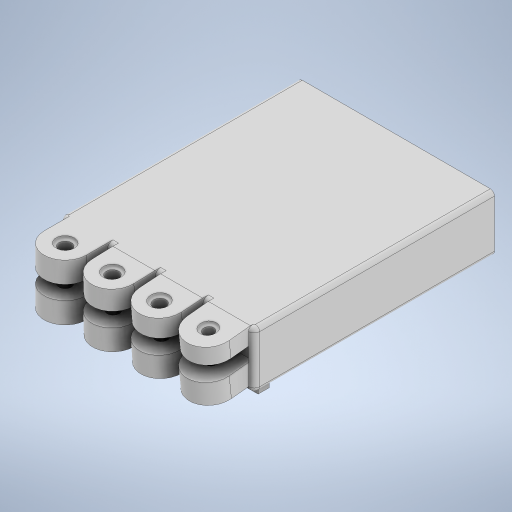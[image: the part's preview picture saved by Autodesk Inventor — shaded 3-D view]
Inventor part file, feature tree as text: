
AUTODESK INVENTOR PART (.ipt)
format: ipt  version: 2024 (Build 280153000, 153)  size: 733,184 bytes
history: native  units: mm
features: sketch x18, extrude x17, fillet x9, other x1
ambient origin geometry x8: Origin, YZ Plane, XZ Plane, XY Plane, X Axis, Y Axis, Z Axis, Center Point
bodies: Body1 (feature_tree)
feature tree (45):
  other  "Твердое тело1"
  extrude  "Выдавливание1"  Depth=20.0mm
  extrude  "Выдавливание2"  Depth=100.0mm
  extrude  "Выдавливание3"  Depth=15.0mm
  extrude  "Выдавливание4"  Depth=5.0mm
  extrude  "Выдавливание5"  Depth=7.5mm
  extrude  "Выдавливание6"  Depth=7.5mm
  extrude  "Выдавливание7"  Depth=15.0mm TaperAngle=0.0deg
  extrude  "Выдавливание8"  Depth=85.0mm
  extrude  "Выдавливание9"  Depth=2.0mm TaperAngle=0.0deg
  extrude  "Выдавливание10"  Depth=15.358897mm
  extrude  "Выдавливание11"  TaperAngle=90.0deg  [1 undecoded]
  sketch  "Эскиз12"
  extrude  "Выдавливание12"  Depth=15.358897mm
  extrude  "Выдавливание13"  Depth=15.0mm
  extrude  "Выдавливание14"  Depth=5.0mm
  extrude  "Выдавливание15"  Depth=7.496951mm
  extrude  "Выдавливание16"  Depth=7.496951mm
  fillet  "Сопряжение1"  Radius=0.349066mm
  fillet  "Сопряжение2"  Radius=15.0mm
  fillet  "Сопряжение3"  Radius=2.0mm
  fillet  "Сопряжение4"  [1 undecoded]
  fillet  "Сопряжение5"  [1 undecoded]
  fillet  "Сопряжение6"  Radius=15.009832mm
  fillet  "Сопряжение7"  Radius=15.009832mm
  fillet  "Сопряжение8"  Radius=5.0mm
  extrude  "Выдавливание17"  Depth=7.5mm
  fillet  "Сопряжение9"  Radius=7.5mm
  sketch  "Эскиз1"
  sketch  "Эскиз2"
  sketch  "Эскиз3"
  sketch  "Эскиз4"
  sketch  "Эскиз5"
  sketch  "Эскиз6"
  sketch  "Эскиз7"
  sketch  "Эскиз8"
  sketch  "Эскиз9"
  sketch  "Эскиз10"
  sketch  "Эскиз11"
  sketch  "Эскиз13"
  sketch  "Эскиз14"
  sketch  "Эскиз15"
  sketch  "Эскиз16"
  sketch  "Эскиз17"
  sketch  "Эскиз18"
note: 3 required parameter values undecoded (feature->parameter linkage not recoverable at this tier; creation-order binding heuristic only, values carry confidence <= 0.55)
